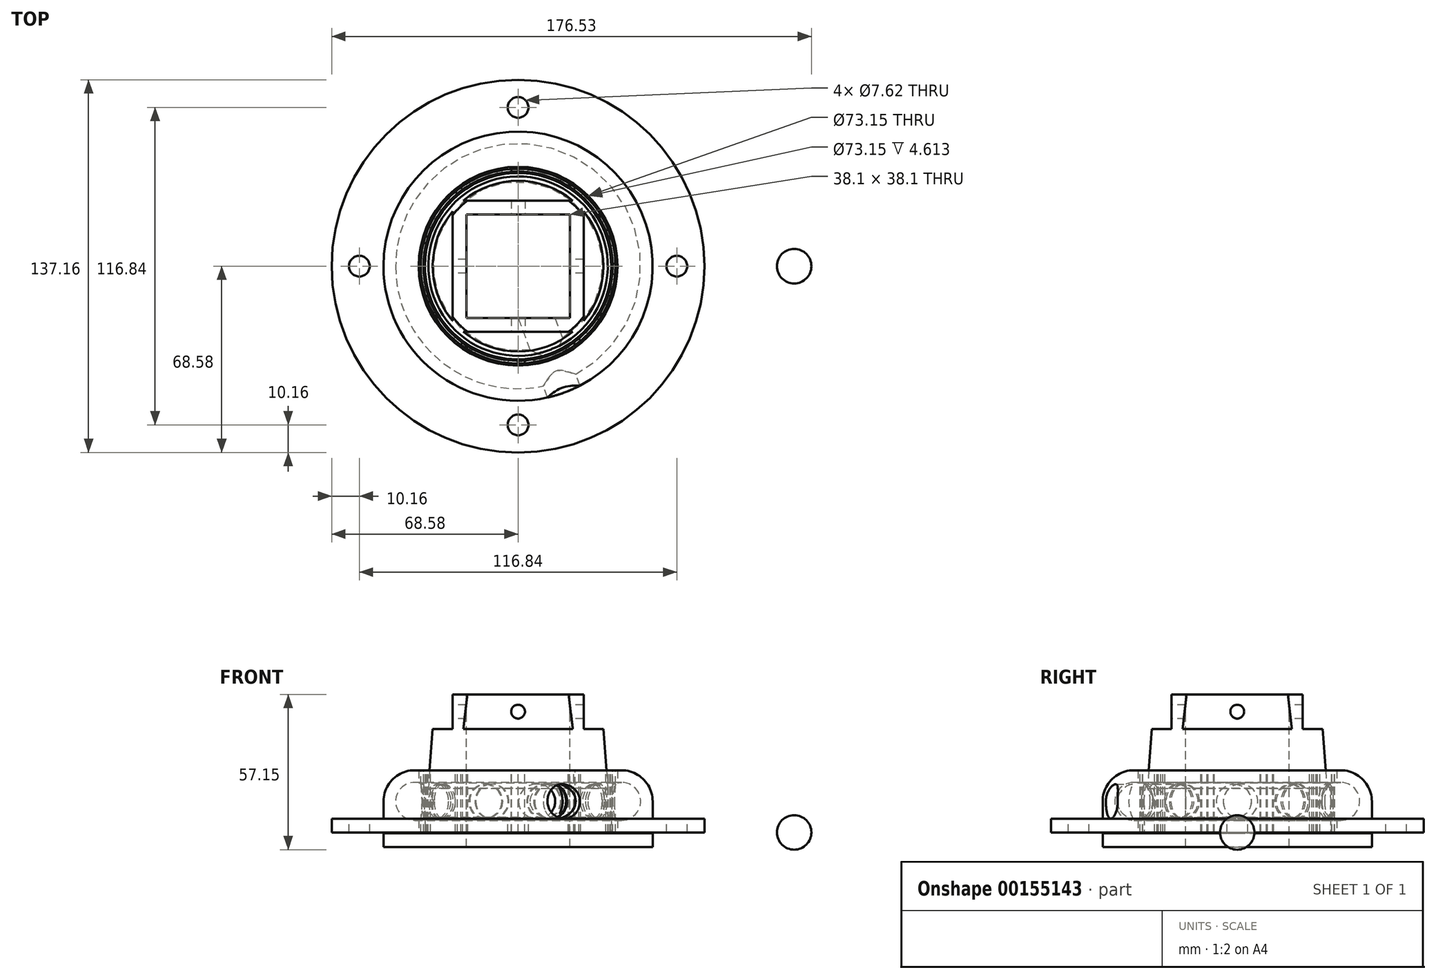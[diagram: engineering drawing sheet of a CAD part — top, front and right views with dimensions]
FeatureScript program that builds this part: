
annotation { "Feature Type Name" : "Feature", "Feature Type Description" : "" }
export const myFeature = defineFeature(function(context is Context, id is Id, definition is map)
    precondition{}
    {
        {
            var Q0;
            Q0=qCreatedBy(makeId("Front.planeOp"),FACE);
            var sketch = newSketch(context, id + "F0", { "sketchPlane" : qUnion([Q0])});
            skLineSegment(sketch, "E0", {"start": v(0, 0) * mm, "end": v(0, 86.97) * mm, "construction": true});
            skLineSegment(sketch, "E1", {"start": v(38.1, 0) * mm, "end": v(49.53, 0) * mm});
            skLineSegment(sketch, "E2", {"start": v(49.53, 5.08) * mm, "end": v(49.53, 22.86) * mm});
            skLineSegment(sketch, "E3", {"start": v(49.53, 22.86) * mm, "end": v(38.1, 22.86) * mm});
            skLineSegment(sketch, "E4", {"start": v(38.1, 22.86) * mm, "end": v(38.1, 0) * mm});
            skCircle(sketch, "E5", {"center": v(38.1, 11.43) * mm, "radius": 6.99 * mm});
            skLineSegment(sketch, "E6", {"start": v(49.53, 0) * mm, "end": v(68.58, 0) * mm});
            skLineSegment(sketch, "E7", {"start": v(68.58, 0) * mm, "end": v(68.58, 5.08) * mm});
            skLineSegment(sketch, "E8", {"start": v(68.58, 5.08) * mm, "end": v(49.53, 5.08) * mm});
            skLineSegment(sketch, "E9.bottom", {"start": v(0, 0) * mm, "end": v(34.3, 0) * mm});
            skLineSegment(sketch, "E9.top", {"start": v(0, 50.8) * mm, "end": v(34.3, 50.8) * mm});
            skLineSegment(sketch, "E9.left", {"start": v(0, 0) * mm, "end": v(0, 50.8) * mm});
            skLineSegment(sketch, "E9.right", {"start": v(34.3, 0) * mm, "end": v(34.3, 50.8) * mm});
            skCircle(sketch, "E10", {"center": v(38.1, 11.43) * mm, "radius": 6.35 * mm, "construction": true});
            skLineSegment(sketch, "E11", {"start": v(34.3, 0) * mm, "end": v(34.3, -0.25) * mm});
            skLineSegment(sketch, "E12", {"start": v(34.3, -0.25) * mm, "end": v(49.53, -0.25) * mm});
            skLineSegment(sketch, "E13", {"start": v(49.53, -0.25) * mm, "end": v(49.53, -5.33) * mm});
            skLineSegment(sketch, "E14", {"start": v(49.53, -5.33) * mm, "end": v(0, -5.33) * mm});
            skLineSegment(sketch, "E15", {"start": v(0, -5.33) * mm, "end": v(0, 0) * mm});
            skLineSegment(sketch, "E16", {"start": v(38.1, 22.86) * mm, "end": v(36.58, 22.86) * mm});
            skLineSegment(sketch, "E17", {"start": v(36.58, 22.86) * mm, "end": v(36.58, 0) * mm});
            skLineSegment(sketch, "E18", {"start": v(36.58, 0) * mm, "end": v(38.1, 0) * mm});
            skArc(sketch, "E19", {"start": v(38.1, 22.86) * mm, "mid": v(46.18, 19.51) * mm, "end": v(49.53, 11.43) * mm});
            skLineSegment(sketch, "E20", {"start": v(33.02, 16.22) * mm, "end": v(30.48, 50.8) * mm});
            skSolve(sketch);
        }
        {
            var Q0;
            {var subQ4=sQuery(id+"F0.wireOp",EDGE,"E1");Q0=makeQuery(id+"F0.imprint","IMPRINT",FACE,{"disambiguationData":[TD([[makeQuery(id+"F0.imprint","IMPRINT",EDGE,{"derivedFrom":subQ4}),1.0]])]});}
            var Q1;
            {var subQ0=sQuery(id+"F0.wireOp",EDGE,"E18");Q1=makeQuery(id+"F0.imprint","IMPRINT",FACE,{"disambiguationData":[TD([[makeQuery(id+"F0.imprint","IMPRINT",EDGE,{"derivedFrom":subQ0}),1.0]])]});}
            var Q2;
            {var subQ0=sQuery(id+"F0.wireOp",EDGE,"E16");Q2=makeQuery(id+"F0.imprint","IMPRINT",FACE,{"disambiguationData":[TD([[makeQuery(id+"F0.imprint","IMPRINT",EDGE,{"derivedFrom":subQ0}),1.0]])]});}
            var Q3;
            Q3=sQuery(id+"F0.wireOp",EDGE,"E0");
            revolve(context, id + "F1", {"entities" : qUnion([Q0, Q1, Q2]), "axis" : qUnion([Q3]), "revolveType" : RevolveType.FULL});
        }
        {
            var Q0;
            Q0=makeQuery(id+"F0.imprint","IMPRINT",FACE,{"disambiguationData":[TD([[makeQuery(id+"F0.imprint","IMPRINT",EDGE,{"derivedFrom":sQuery(id+"F0.wireOp",EDGE,"E9.bottom")}),1.0]])]});
            var Q1;
            Q1=makeQuery(id+"F0.imprint","IMPRINT",FACE,{"disambiguationData":[TD([[makeQuery(id+"F0.imprint","IMPRINT",EDGE,{"derivedFrom":sQuery(id+"F0.wireOp",EDGE,"E9.bottom")}),-1.0]])]});
            var Q2;
            Q2=sQuery(id+"F0.wireOp",EDGE,"E0");
            revolve(context, id + "F2", {"entities" : qUnion([Q0, Q1]), "axis" : qUnion([Q2]), "revolveType" : RevolveType.FULL});
        }
        {
            var Q0;
            Q0=makeQuery(id+"F2.opRevolve","SWEPT_FACE",FACE,{"disambiguationData":[OSD([sQuery(id+"F0.wireOp",EDGE,"E9.top")])]});
            var sketch = newSketch(context, id + "F3", { "sketchPlane" : qUnion([Q0])});
            skLineSegment(sketch, "E21.bottom", {"start": v(-19.05, -19.05) * mm, "end": v(19.05, -19.05) * mm});
            skLineSegment(sketch, "E21.top", {"start": v(-19.05, 19.05) * mm, "end": v(19.05, 19.05) * mm});
            skLineSegment(sketch, "E21.left", {"start": v(-19.05, -19.05) * mm, "end": v(-19.05, 19.05) * mm});
            skLineSegment(sketch, "E21.right", {"start": v(19.05, -19.05) * mm, "end": v(19.05, 19.05) * mm});
            skLineSegment(sketch, "E22", {"start": v(0, 0) * mm, "end": v(0, 31.24) * mm, "construction": true});
            skLineSegment(sketch, "E23", {"start": v(0, 0) * mm, "end": v(31.24, 0) * mm, "construction": true});
            skCircle(sketch, "E24.0", {"center": v(0, 0) * mm, "radius": 33.02 * mm});
            skLineSegment(sketch, "E25", {"start": v(-22.54, 24.13) * mm, "end": v(22.54, 24.13) * mm});
            skLineSegment(sketch, "E26", {"start": v(-22.54, -24.13) * mm, "end": v(22.54, -24.13) * mm});
            skLineSegment(sketch, "E27", {"start": v(24.13, -22.54) * mm, "end": v(24.13, 22.54) * mm});
            skLineSegment(sketch, "E28", {"start": v(-24.13, -22.54) * mm, "end": v(-24.13, 22.54) * mm});
            skSolve(sketch);
        }
        {
            var Q0;
            Q0=makeQuery(id+"F3.imprint","IMPRINT",FACE,{"disambiguationData":[TD([[makeQuery(id+"F3.imprint","IMPRINT",EDGE,{"derivedFrom":sQuery(id+"F3.wireOp",EDGE,"E21.bottom")}),1.0]])]});
            extrude(context, id + "F4", {"entities" : qUnion([Q0]), "operationType" : NewBodyOperationType.REMOVE, "endBound" : BoundingType.THROUGH_ALL, "oppositeDirection" : true, "depth" : 25.4 * mm});
        }
        {
            var Q0;
            {var subQ0=sQuery(id+"F3.wireOp",EDGE,"E25");Q0=makeQuery(id+"F3.imprint","IMPRINT",FACE,{"disambiguationData":[TD([[makeQuery(id+"F3.imprint","IMPRINT",EDGE,{"derivedFrom":subQ0}),1.0]])]});}
            var Q1;
            {var subQ0=sQuery(id+"F3.wireOp",EDGE,"E27");Q1=makeQuery(id+"F3.imprint","IMPRINT",FACE,{"disambiguationData":[TD([[makeQuery(id+"F3.imprint","IMPRINT",EDGE,{"derivedFrom":subQ0}),-1.0]])]});}
            var Q2;
            {var subQ0=sQuery(id+"F3.wireOp",EDGE,"E26");Q2=makeQuery(id+"F3.imprint","IMPRINT",FACE,{"disambiguationData":[TD([[makeQuery(id+"F3.imprint","IMPRINT",EDGE,{"derivedFrom":subQ0}),-1.0]])]});}
            var Q3;
            {var subQ0=sQuery(id+"F3.wireOp",EDGE,"E28");Q3=makeQuery(id+"F3.imprint","IMPRINT",FACE,{"disambiguationData":[TD([[makeQuery(id+"F3.imprint","IMPRINT",EDGE,{"derivedFrom":subQ0}),1.0]])]});}
            var Q4;
            {var subQ0=sQuery(id+"F3.wireOp",EDGE,"E25");var subQ1=makeQuery(id+"F2.opRevolve","SWEPT_EDGE",EDGE,{"disambiguationData":[OSD([sQuery(id+"F0.wireOp",EDGE,"E9.top"),sQuery(id+"F0.wireOp",EDGE,"E20")])]});var subQ2=makeQuery(id+"F3.imprint","INTERSECT",VERTEX,{"disambiguationData":[OD(0.0)],"derivedFrom":[subQ1,subQ0]});Q4=makeQuery(id+"F3.imprint","IMPRINT",FACE,{"disambiguationData":[TD([[makeQuery(id+"F3.imprint","IMPRINT",EDGE,{"disambiguationData":[TD([[subQ2,-1.0]])],"derivedFrom":subQ0}),1.0]])]});}
            var Q5;
            {var subQ0=sQuery(id+"F3.wireOp",EDGE,"E27");var subQ1=makeQuery(id+"F2.opRevolve","SWEPT_EDGE",EDGE,{"disambiguationData":[OSD([sQuery(id+"F0.wireOp",EDGE,"E9.top"),sQuery(id+"F0.wireOp",EDGE,"E20")])]});var subQ2=makeQuery(id+"F3.imprint","INTERSECT",VERTEX,{"disambiguationData":[OD(0.0)],"derivedFrom":[subQ1,subQ0]});Q5=makeQuery(id+"F3.imprint","IMPRINT",FACE,{"disambiguationData":[TD([[makeQuery(id+"F3.imprint","IMPRINT",EDGE,{"disambiguationData":[TD([[subQ2,-1.0]])],"derivedFrom":subQ0}),-1.0]])]});}
            var Q6;
            {var subQ0=sQuery(id+"F3.wireOp",EDGE,"E26");var subQ1=makeQuery(id+"F2.opRevolve","SWEPT_EDGE",EDGE,{"disambiguationData":[OSD([sQuery(id+"F0.wireOp",EDGE,"E9.top"),sQuery(id+"F0.wireOp",EDGE,"E20")])]});var subQ2=makeQuery(id+"F3.imprint","INTERSECT",VERTEX,{"disambiguationData":[OD(0.0)],"derivedFrom":[subQ1,subQ0]});Q6=makeQuery(id+"F3.imprint","IMPRINT",FACE,{"disambiguationData":[TD([[makeQuery(id+"F3.imprint","IMPRINT",EDGE,{"disambiguationData":[TD([[subQ2,-1.0]])],"derivedFrom":subQ0}),-1.0]])]});}
            var Q7;
            {var subQ0=sQuery(id+"F3.wireOp",EDGE,"E28");var subQ1=makeQuery(id+"F2.opRevolve","SWEPT_EDGE",EDGE,{"disambiguationData":[OSD([sQuery(id+"F0.wireOp",EDGE,"E9.top"),sQuery(id+"F0.wireOp",EDGE,"E20")])]});var subQ2=makeQuery(id+"F3.imprint","INTERSECT",VERTEX,{"disambiguationData":[OD(0.0)],"derivedFrom":[subQ1,subQ0]});Q7=makeQuery(id+"F3.imprint","IMPRINT",FACE,{"disambiguationData":[TD([[makeQuery(id+"F3.imprint","IMPRINT",EDGE,{"disambiguationData":[TD([[subQ2,-1.0]])],"derivedFrom":subQ0}),1.0]])]});}
            extrude(context, id + "F5", {"entities" : qUnion([Q0, Q1, Q2, Q3, Q4, Q5, Q6, Q7]), "operationType" : NewBodyOperationType.REMOVE, "oppositeDirection" : true, "depth" : 12.7 * mm});
        }
        {
            var Q0;
            Q0=makeQuery(id+"F1.opRevolve","SWEPT_FACE",FACE,{"disambiguationData":[OSD([sQuery(id+"F0.wireOp",EDGE,"E8")])]});
            var sketch = newSketch(context, id + "F6", { "sketchPlane" : qUnion([Q0])});
            skCircle(sketch, "E29", {"center": v(0, 58.42) * mm, "radius": 3.81 * mm});
            skLineSegment(sketch, "E30", {"start": v(0, 0) * mm, "end": v(0, 58.42) * mm, "construction": true});
            skLineSegment(sketch, "E31", {"start": v(0, 0) * mm, "end": v(58.42, 0) * mm, "construction": true});
            skLineSegment(sketch, "E32", {"start": v(0, 0) * mm, "end": v(0, -58.42) * mm, "construction": true});
            skLineSegment(sketch, "E33", {"start": v(0, 0) * mm, "end": v(-58.42, 0) * mm, "construction": true});
            skCircle(sketch, "E34", {"center": v(58.42, 0) * mm, "radius": 3.81 * mm});
            skCircle(sketch, "E35", {"center": v(0, -58.42) * mm, "radius": 3.81 * mm});
            skCircle(sketch, "E36", {"center": v(-58.42, 0) * mm, "radius": 3.81 * mm});
            skSolve(sketch);
        }
        {
            var Q0;
            Q0=makeQuery(id+"F6.imprint","IMPRINT",FACE,{"disambiguationData":[TD([[makeQuery(id+"F6.imprint","IMPRINT",EDGE,{"derivedFrom":sQuery(id+"F6.wireOp",EDGE,"E29")}),1.0]])]});
            var Q1;
            Q1=makeQuery(id+"F6.imprint","IMPRINT",FACE,{"disambiguationData":[TD([[makeQuery(id+"F6.imprint","IMPRINT",EDGE,{"derivedFrom":sQuery(id+"F6.wireOp",EDGE,"E34")}),1.0]])]});
            var Q2;
            Q2=makeQuery(id+"F6.imprint","IMPRINT",FACE,{"disambiguationData":[TD([[makeQuery(id+"F6.imprint","IMPRINT",EDGE,{"derivedFrom":sQuery(id+"F6.wireOp",EDGE,"E35")}),1.0]])]});
            var Q3;
            Q3=makeQuery(id+"F6.imprint","IMPRINT",FACE,{"disambiguationData":[TD([[makeQuery(id+"F6.imprint","IMPRINT",EDGE,{"derivedFrom":sQuery(id+"F6.wireOp",EDGE,"E36")}),1.0]])]});
            extrude(context, id + "F7", {"entities" : qUnion([Q0, Q1, Q2, Q3]), "operationType" : NewBodyOperationType.REMOVE, "endBound" : BoundingType.THROUGH_ALL, "oppositeDirection" : true, "depth" : 25.4 * mm});
        }
        {
            var Q0;
            Q0=qCreatedBy(makeId("Front.planeOp"),FACE);
            var sketch = newSketch(context, id + "F8", { "sketchPlane" : qUnion([Q0])});
            skArc(sketch, "E37", {"start": v(101.6, -6.35) * mm, "mid": v(107.95, 0) * mm, "end": v(101.6, 6.35) * mm});
            skLineSegment(sketch, "E38", {"start": v(101.6, -14.31) * mm, "end": v(101.6, 21.94) * mm, "construction": true});
            skLineSegment(sketch, "E39", {"start": v(101.6, 6.35) * mm, "end": v(101.6, -6.35) * mm});
            skSolve(sketch);
        }
        {
            var Q0;
            Q0=makeQuery(id+"F8.imprint","IMPRINT",FACE,{"disambiguationData":[TD([[makeQuery(id+"F8.imprint","IMPRINT",EDGE,{"derivedFrom":sQuery(id+"F8.wireOp",EDGE,"E37")}),1.0]])]});
            var Q1;
            Q1=sQuery(id+"F8.wireOp",EDGE,"E38");
            revolve(context, id + "F9", {"entities" : qUnion([Q0]), "axis" : qUnion([Q1]), "revolveType" : RevolveType.FULL});
        }
        {
            var Q0;
            Q0=sQuery(id+"F0.wireOp",VERTEX,"E10.center");
            var Q1;
            Q1=qCreatedBy(makeId("Top.planeOp"),FACE);
            cPlane(context, id + "F10", {"entities" : qUnion([Q0, Q1]), "cplaneType" : CPlaneType.PLANE_POINT, "offset" : 25.4 * mm, "width" : 152.4 * mm, "height" : 152.4 * mm});
        }
        {
            var Q0;
            Q0=qCreatedBy(id+"F10.planeOp",FACE);
            var sketch = newSketch(context, id + "F11", { "sketchPlane" : qUnion([Q0])});
            skLineSegment(sketch, "E40", {"start": v(0, 0) * mm, "end": v(37.92, 0) * mm, "construction": true});
            skLineSegment(sketch, "E41.1.0", {"start": v(0, 0) * mm, "end": v(30.68, 22.29) * mm, "construction": true});
            skLineSegment(sketch, "E41.2.0", {"start": v(0, 0) * mm, "end": v(11.72, 36.06) * mm, "construction": true});
            skLineSegment(sketch, "E41.3.0", {"start": v(0, 0) * mm, "end": v(-11.72, 36.06) * mm, "construction": true});
            skLineSegment(sketch, "E41.4.0", {"start": v(0, 0) * mm, "end": v(-30.68, 22.29) * mm, "construction": true});
            skLineSegment(sketch, "E41.5.0", {"start": v(0, 0) * mm, "end": v(-37.92, 0) * mm, "construction": true});
            skLineSegment(sketch, "E41.6.0", {"start": v(0, 0) * mm, "end": v(-30.68, -22.29) * mm, "construction": true});
            skLineSegment(sketch, "E41.7.0", {"start": v(0, 0) * mm, "end": v(-11.72, -36.06) * mm, "construction": true});
            skLineSegment(sketch, "E41.8.0", {"start": v(0, 0) * mm, "end": v(11.72, -36.06) * mm, "construction": true});
            skLineSegment(sketch, "E41.9.0", {"start": v(0, 0) * mm, "end": v(30.68, -22.29) * mm, "construction": true});
            skPoint(sketch, "E41.center", {"position": v(0, 0) * mm});
            skSolve(sketch);
        }
        {
            var Q0;
            Q0=sQuery(id+"F0.wireOp",EDGE,"E0");
            var Q1;
            Q1=qCreatedBy(makeId("Front.planeOp"),FACE);
            cPlane(context, id + "F12", {"entities" : qUnion([Q0, Q1]), "cplaneType" : CPlaneType.LINE_ANGLE, "offset" : 25.4 * mm, "angle" : 20 * degree, "width" : 152.4 * mm, "height" : 152.4 * mm});
        }
        {
            var Q0;
            Q0=makeQuery(id+"F1.opRevolve","SWEPT_FACE",FACE,{"disambiguationData":[OSD([sQuery(id+"F0.wireOp",EDGE,"E3"),sQuery(id+"F0.wireOp",EDGE,"E16")])]});
            var sketch = newSketch(context, id + "F13", { "sketchPlane" : qUnion([Q0])});
            skCircle(sketch, "E42.0", {"center": v(0, 0) * mm, "radius": 35.81 * mm});
            skCircle(sketch, "E43", {"center": v(0, 0) * mm, "radius": 34.8 * mm});
            skLineSegment(sketch, "E44", {"start": v(0, 0) * mm, "end": v(16.94, -46.54) * mm, "construction": true});
            skLineSegment(sketch, "E45", {"start": v(0, 0) * mm, "end": v(0, -36.58) * mm});
            skLineSegment(sketch, "E46.MirrorCS", {"start": v(0, 0) * mm, "end": v(23.51, -28.02) * mm});
            skSolve(sketch);
        }
        {
            var Q0;
            {var subQ0=sQuery(id+"F13.wireOp",EDGE,"E45");var subQ1=sQuery(id+"F13.wireOp",EDGE,"E42.0");var subQ2=makeQuery(id+"F13.imprint","INTERSECT",VERTEX,{"derivedFrom":[subQ1,subQ0]});Q0=makeQuery(id+"F13.imprint","IMPRINT",FACE,{"disambiguationData":[TD([[makeQuery(id+"F13.imprint","IMPRINT",EDGE,{"disambiguationData":[TD([[subQ2,-1.0]])],"derivedFrom":subQ1}),1.0]])]});}
            var Q1;
            Q1=makeQuery(id+"F1.opRevolve","SWEPT_FACE",FACE,{"disambiguationData":[OSD([sQuery(id+"F0.wireOp",EDGE,"E1"),sQuery(id+"F0.wireOp",EDGE,"E6"),sQuery(id+"F0.wireOp",EDGE,"E18")])]});
            extrude(context, id + "F14", {"entities" : qUnion([Q0]), "endBound" : BoundingType.UP_TO_SURFACE, "oppositeDirection" : true, "endBoundEntityFace" : qUnion([Q1]), "depth" : 25.4 * mm});
        }
        {
            var Q0;
            Q0=qCreatedBy(id+"F12.planeOp",FACE);
            var sketch = newSketch(context, id + "F15", { "sketchPlane" : qUnion([Q0])});
            skCircle(sketch, "E47", {"center": v(0, 11.43) * mm, "radius": 6.35 * mm});
            skSolve(sketch);
        }
        {
            var Q0;
            Q0=makeQuery(id+"F15.imprint","IMPRINT",FACE,{"disambiguationData":[TD([[makeQuery(id+"F15.imprint","IMPRINT",EDGE,{"derivedFrom":sQuery(id+"F15.wireOp",EDGE,"E47")}),1.0]])]});
            var Q1;
            Q1=makeQuery(id+"F14.opExtrude","SWEPT_BODY",BODY,{"disambiguationData":[OSD([sQuery(id+"F13.wireOp",EDGE,"E42.0"),sQuery(id+"F13.wireOp",EDGE,"E43")])]});
            extrude(context, id + "F16", {"entities" : qUnion([Q0]), "operationType" : NewBodyOperationType.REMOVE, "endBound" : BoundingType.THROUGH_ALL, "oppositeDirection" : true, "endBoundEntityBody" : qUnion([Q1]), "depth" : 25.4 * mm});
        }
        {
            var Q0;
            Q0=makeQuery(id+"F14.opExtrude","SWEPT_BODY",BODY,{"disambiguationData":[OSD([sQuery(id+"F13.wireOp",EDGE,"E42.0"),sQuery(id+"F13.wireOp",EDGE,"E43")])]});
            var Q1;
            Q1=sQuery(id+"F0.wireOp",EDGE,"E0");
            circularPattern(context, id + "F17", {"operationType" : NewBodyOperationType.ADD, "entities" : qUnion([Q0]), "axis" : qUnion([Q1]), "angle" : 360 * degree, "instanceCount" : 10, "equalSpace" : true});
        }
        {
            var Q0;
            Q0=qCreatedBy(makeId("Front.planeOp"),FACE);
            var sketch = newSketch(context, id + "F18", { "sketchPlane" : qUnion([Q0])});
            skCircle(sketch, "E48", {"center": v(0, 44.45) * mm, "radius": 2.54 * mm});
            skSolve(sketch);
        }
        {
            var Q0;
            Q0=makeQuery(id+"F18.imprint","IMPRINT",FACE,{"disambiguationData":[TD([[makeQuery(id+"F18.imprint","IMPRINT",EDGE,{"derivedFrom":sQuery(id+"F18.wireOp",EDGE,"E48")}),1.0]])]});
            extrude(context, id + "F19", {"entities" : qUnion([Q0]), "operationType" : NewBodyOperationType.REMOVE, "endBound" : BoundingType.THROUGH_ALL, "oppositeDirection" : true, "depth" : 25.4 * mm, "hasSecondDirection" : true, "secondDirectionBound" : SecondDirectionBoundingType.THROUGH_ALL, "secondDirectionOppositeDirection" : false, "secondDirectionDepth" : 25.4 * mm});
        }
        {
            var Q0;
            Q0=qCreatedBy(makeId("Right.planeOp"),FACE);
            var sketch = newSketch(context, id + "F20", { "sketchPlane" : qUnion([Q0])});
            skCircle(sketch, "E49", {"center": v(0, 44.45) * mm, "radius": 2.54 * mm});
            skSolve(sketch);
        }
        {
            var Q0;
            Q0=makeQuery(id+"F20.imprint","IMPRINT",FACE,{"disambiguationData":[TD([[makeQuery(id+"F20.imprint","IMPRINT",EDGE,{"derivedFrom":sQuery(id+"F20.wireOp",EDGE,"E49")}),1.0]])]});
            extrude(context, id + "F21", {"entities" : qUnion([Q0]), "operationType" : NewBodyOperationType.REMOVE, "endBound" : BoundingType.THROUGH_ALL, "depth" : 25.4 * mm, "hasSecondDirection" : true, "secondDirectionBound" : SecondDirectionBoundingType.THROUGH_ALL, "secondDirectionOppositeDirection" : true, "secondDirectionDepth" : 25.4 * mm});
        }
    });
